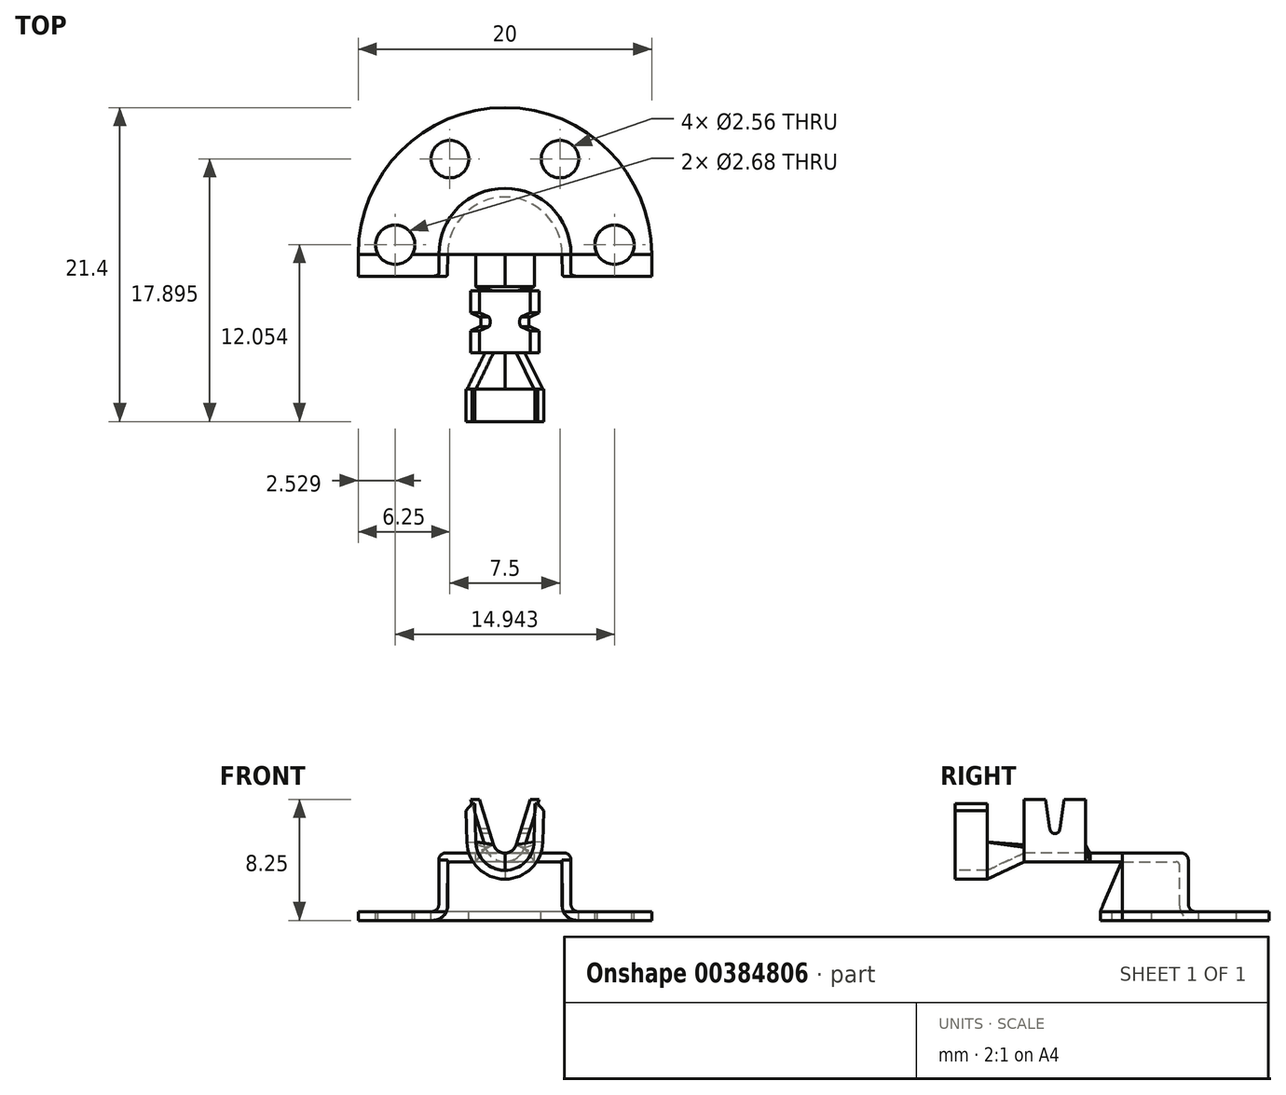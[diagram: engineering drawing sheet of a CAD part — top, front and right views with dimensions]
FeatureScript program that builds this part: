
annotation { "Feature Type Name" : "Feature", "Feature Type Description" : "" }
export const myFeature = defineFeature(function(context is Context, id is Id, definition is map)
    precondition{}
    {
        {
            var Q0;
            Q0=qCreatedBy(makeId("Front.planeOp"),FACE);
            var sketch = newSketch(context, id + "F0", { "sketchPlane" : qUnion([Q0])});
            skArc(sketch, "E0", {"start": v(-1.98, -0.05) * mm, "mid": v(0, -1.98) * mm, "end": v(1.98, -0.05) * mm});
            skArc(sketch, "E1", {"start": v(-2.58, -0.06) * mm, "mid": v(0, -2.58) * mm, "end": v(2.58, -0.06) * mm});
            skLineSegment(sketch, "E2", {"start": v(2.58, -0.06) * mm, "end": v(2.64, 2.08) * mm});
            skLineSegment(sketch, "E3", {"start": v(1.98, -0.05) * mm, "end": v(2.05, 2.57) * mm});
            skLineSegment(sketch, "E4", {"start": v(2.05, 2.57) * mm, "end": v(2.25, 2.56) * mm});
            skLineSegment(sketch, "E5.MirrorCS", {"start": v(-1.98, -0.05) * mm, "end": v(-2.05, 2.57) * mm});
            skLineSegment(sketch, "E6.MirrorCS", {"start": v(-2.58, -0.06) * mm, "end": v(-2.64, 2.08) * mm});
            skLineSegment(sketch, "E7.MirrorCS", {"start": v(-2.25, 2.56) * mm, "end": v(-2.64, 2.08) * mm});
            skLineSegment(sketch, "E8.MirrorCS", {"start": v(-2.05, 2.57) * mm, "end": v(-2.25, 2.56) * mm});
            skPoint(sketch, "E9", {"position": v(0, -2.58) * mm});
            skLineSegment(sketch, "E10", {"start": v(2.25, 2.56) * mm, "end": v(2.64, 2.08) * mm});
            skSolve(sketch);
        }
        {
            var Q0;
            Q0=makeQuery(id+"F0.imprint","IMPRINT",FACE,{"disambiguationData":[TD([[makeQuery(id+"F0.imprint","IMPRINT",EDGE,{"derivedFrom":sQuery(id+"F0.wireOp",EDGE,"E0")}),-1.0]])]});
            extrude(context, id + "F1", {"entities" : qUnion([Q0]), "oppositeDirection" : true, "depth" : 2.2 * mm});
        }
        {
            var Q0;
            Q0=makeQuery(id+"F1.opExtrude","CAP_FACE",FACE,{"disambiguationData":[OSD([sQuery(id+"F0.wireOp",EDGE,"E0"),sQuery(id+"F0.wireOp",EDGE,"E1"),sQuery(id+"F0.wireOp",EDGE,"E2"),sQuery(id+"F0.wireOp",EDGE,"E3"),sQuery(id+"F0.wireOp",EDGE,"E4"),sQuery(id+"F0.wireOp",EDGE,"E5.MirrorCS"),sQuery(id+"F0.wireOp",EDGE,"E6.MirrorCS"),sQuery(id+"F0.wireOp",EDGE,"E7.MirrorCS"),sQuery(id+"F0.wireOp",EDGE,"E8.MirrorCS"),sQuery(id+"F0.wireOp",EDGE,"E10")])],"isStart":false});
            cPlane(context, id + "F2", {"entities" : qUnion([Q0]), "cplaneType" : CPlaneType.OFFSET, "offset" : 2.5 * mm, "width" : 150 * mm, "height" : 150 * mm});
        }
        {
            var Q0;
            Q0=qCreatedBy(id+"F2.planeOp",FACE);
            var sketch = newSketch(context, id + "F3", { "sketchPlane" : qUnion([Q0])});
            skArc(sketch, "E11.converted", {"start": v(-0.77, -0.24) * mm, "mid": v(0, -0.8) * mm, "end": v(0.77, -0.24) * mm});
            skArc(sketch, "E12.converted", {"start": v(-1.34, -0.41) * mm, "mid": v(0, -1.4) * mm, "end": v(1.34, -0.41) * mm});
            skLineSegment(sketch, "E13", {"start": v(1.34, -0.41) * mm, "end": v(2.34, 2.85) * mm});
            skLineSegment(sketch, "E14", {"start": v(0.77, -0.24) * mm, "end": v(1.73, 2.85) * mm});
            skLineSegment(sketch, "E15", {"start": v(1.72, 2.85) * mm, "end": v(2.34, 2.85) * mm});
            skLineSegment(sketch, "E16", {"start": v(-2.74, -1.4) * mm, "end": v(2.74, -1.4) * mm, "construction": true});
            skLineSegment(sketch, "E17.MirrorCS", {"start": v(-0.77, -0.24) * mm, "end": v(-1.73, 2.85) * mm});
            skLineSegment(sketch, "E18.MirrorCS", {"start": v(-1.34, -0.41) * mm, "end": v(-2.34, 2.85) * mm});
            skLineSegment(sketch, "E19.MirrorCS", {"start": v(-1.72, 2.85) * mm, "end": v(-2.34, 2.85) * mm});
            skPoint(sketch, "E20.orphan", {"position": v(2.1, 2.04) * mm});
            skPoint(sketch, "E21.orphan", {"position": v(-2.1, 2.04) * mm});
            skSolve(sketch);
        }
        {
            var Q0;
            Q0=qSketchRegion(id+"F3",true);
            extrude(context, id + "F4", {"entities" : qUnion([Q0]), "depth" : 4.2 * mm});
        }
        {
            var Q0;
            Q0=makeQuery(id+"F4.opExtrude","CAP_FACE",FACE,{"disambiguationData":[OSD([sQuery(id+"F3.wireOp",EDGE,"E11.converted"),sQuery(id+"F3.wireOp",EDGE,"E12.converted"),sQuery(id+"F3.wireOp",EDGE,"E13"),sQuery(id+"F3.wireOp",EDGE,"E14"),sQuery(id+"F3.wireOp",EDGE,"E15"),sQuery(id+"F3.wireOp",EDGE,"JUiI4d2J-rTaX-Cvjk-MSou-KpunC5FrSqzR"),sQuery(id+"F3.wireOp",EDGE,"E17.MirrorCS"),sQuery(id+"F3.wireOp",EDGE,"E18.MirrorCS"),sQuery(id+"F3.wireOp",EDGE,"aa090b4b-4b93-4f69-ac82-eb0763e6126e0.MirrorCS"),sQuery(id+"F3.wireOp",EDGE,"E19.MirrorCS")])],"isStart":true});
            var sketch = newSketch(context, id + "F5", { "sketchPlane" : qUnion([Q0])});
            skArc(sketch, "E22", {"start": v(0, -0.81) * mm, "mid": v(0.48, -0.65) * mm, "end": v(0.77, -0.24) * mm});
            skArc(sketch, "E23", {"start": v(0, -1.41) * mm, "mid": v(0.84, -1.13) * mm, "end": v(1.35, -0.41) * mm});
            skLineSegment(sketch, "E24", {"start": v(0.77, -0.24) * mm, "end": v(1.35, -0.41) * mm});
            skLineSegment(sketch, "E25", {"start": v(0, 0) * mm, "end": v(0, -1.92) * mm, "construction": true});
            skLineSegment(sketch, "E26", {"start": v(0, -0.81) * mm, "end": v(0, -1.41) * mm});
            skSolve(sketch);
        }
        {
            var Q0;
            Q0=makeQuery(id+"F1.opExtrude","CAP_FACE",FACE,{"disambiguationData":[OSD([sQuery(id+"F0.wireOp",EDGE,"E0"),sQuery(id+"F0.wireOp",EDGE,"E1"),sQuery(id+"F0.wireOp",EDGE,"E2"),sQuery(id+"F0.wireOp",EDGE,"E3"),sQuery(id+"F0.wireOp",EDGE,"E4"),sQuery(id+"F0.wireOp",EDGE,"E5.MirrorCS"),sQuery(id+"F0.wireOp",EDGE,"E6.MirrorCS"),sQuery(id+"F0.wireOp",EDGE,"E7.MirrorCS"),sQuery(id+"F0.wireOp",EDGE,"E8.MirrorCS"),sQuery(id+"F0.wireOp",EDGE,"E10")])],"isStart":false});
            var sketch = newSketch(context, id + "F6", { "sketchPlane" : qUnion([Q0])});
            skArc(sketch, "E27", {"start": v(-1.98, -0.05) * mm, "mid": v(-1.39, -1.42) * mm, "end": v(0, -1.98) * mm});
            skArc(sketch, "E28", {"start": v(-2.58, -0.06) * mm, "mid": v(-1.8, -1.85) * mm, "end": v(0, -2.58) * mm});
            skLineSegment(sketch, "E29", {"start": v(-2.58, -0.06) * mm, "end": v(-1.98, -0.05) * mm});
            skLineSegment(sketch, "E30", {"start": v(0, 0) * mm, "end": v(0, -2.84) * mm, "construction": true});
            skPoint(sketch, "E30.endSnap0", {"position": v(0, -1.98) * mm});
            skLineSegment(sketch, "E31", {"start": v(0, -1.99) * mm, "end": v(0, -2.58) * mm});
            skSolve(sketch);
        }
        {
            var Q0;
            Q0=qSketchRegion(id+"F5",true);
            var Q1;
            Q1=qSketchRegion(id+"F6",true);
            loft(context, id + "F7", {"sheetProfilesArray" : [{ "sheetProfileEntities" : qUnion([Q0]) }, { "sheetProfileEntities" : qUnion([Q1]) }]});
        }
        {
            var Q0;
            {var subQ0=sQuery(id+"F5.wireOp",EDGE,"E23");Q0=makeQuery(id+"F7.opLoft","SWEPT_BODY",BODY,{"disambiguationData":[OSD([makeQuery(id+"F5.imprint","IMPRINT",FACE,{"disambiguationData":[TD([[makeQuery(id+"F5.imprint","IMPRINT",EDGE,{"derivedFrom":subQ0}),1.0]])]}),makeQuery(id+"F6.imprint","IMPRINT",FACE,{"disambiguationData":[TD([[makeQuery(id+"F6.imprint","IMPRINT",EDGE,{"derivedFrom":sQuery(id+"F6.wireOp",EDGE,"E27")}),1.0]])]})])]});}
            var Q1;
            Q1=qCreatedBy(makeId("Right.planeOp"),FACE);
            mirror(context, id + "F8", {"entities" : qUnion([Q0]), "mirrorPlane" : qUnion([Q1])});
        }
        {
            var Q0;
            Q0=makeQuery(id+"F4.opExtrude","CAP_FACE",FACE,{"disambiguationData":[OSD([sQuery(id+"F3.wireOp",EDGE,"E11.converted"),sQuery(id+"F3.wireOp",EDGE,"E12.converted"),sQuery(id+"F3.wireOp",EDGE,"E13"),sQuery(id+"F3.wireOp",EDGE,"E14"),sQuery(id+"F3.wireOp",EDGE,"E15"),sQuery(id+"F3.wireOp",EDGE,"JUiI4d2J-rTaX-Cvjk-MSou-KpunC5FrSqzR"),sQuery(id+"F3.wireOp",EDGE,"E17.MirrorCS"),sQuery(id+"F3.wireOp",EDGE,"E18.MirrorCS"),sQuery(id+"F3.wireOp",EDGE,"aa090b4b-4b93-4f69-ac82-eb0763e6126e0.MirrorCS"),sQuery(id+"F3.wireOp",EDGE,"E19.MirrorCS")])],"isStart":false});
            cPlane(context, id + "F9", {"entities" : qUnion([Q0]), "cplaneType" : CPlaneType.OFFSET, "offset" : .3 * mm, "width" : 150 * mm, "height" : 150 * mm});
        }
        {
            var Q0;
            Q0=qCreatedBy(id+"F9.planeOp",FACE);
            var sketch = newSketch(context, id + "F10", { "sketchPlane" : qUnion([Q0])});
            skLineSegment(sketch, "E32", {"start": v(0, -0.8) * mm, "end": v(0, -1.4) * mm, "construction": true});
            skLineSegment(sketch, "E33", {"start": v(0, -0.8) * mm, "end": v(0, -1.4) * mm});
            skLineSegment(sketch, "E34.MirrorCS", {"start": v(0, -1.4) * mm, "end": v(2, -1.4) * mm});
            skLineSegment(sketch, "E35.MirrorCS", {"start": v(2, -1.4) * mm, "end": v(2, -0.8) * mm});
            skLineSegment(sketch, "E36.MirrorCS", {"start": v(0, -0.8) * mm, "end": v(2, -0.8) * mm});
            skSolve(sketch);
        }
        {
            var Q0;
            Q0=makeQuery(id+"F4.opExtrude","CAP_FACE",FACE,{"disambiguationData":[OSD([sQuery(id+"F3.wireOp",EDGE,"E11.converted"),sQuery(id+"F3.wireOp",EDGE,"E12.converted"),sQuery(id+"F3.wireOp",EDGE,"E13"),sQuery(id+"F3.wireOp",EDGE,"E14"),sQuery(id+"F3.wireOp",EDGE,"E15"),sQuery(id+"F3.wireOp",EDGE,"JUiI4d2J-rTaX-Cvjk-MSou-KpunC5FrSqzR"),sQuery(id+"F3.wireOp",EDGE,"E17.MirrorCS"),sQuery(id+"F3.wireOp",EDGE,"E18.MirrorCS"),sQuery(id+"F3.wireOp",EDGE,"aa090b4b-4b93-4f69-ac82-eb0763e6126e0.MirrorCS"),sQuery(id+"F3.wireOp",EDGE,"E19.MirrorCS")])],"isStart":false});
            var sketch = newSketch(context, id + "F11", { "sketchPlane" : qUnion([Q0])});
            skLineSegment(sketch, "E37", {"start": v(0, 0) * mm, "end": v(0, -1.83) * mm, "construction": true});
            skPoint(sketch, "E37.endSnap0", {"position": v(0, -0.8) * mm});
            skLineSegment(sketch, "E38", {"start": v(0, -0.81) * mm, "end": v(0, -1.41) * mm});
            skLineSegment(sketch, "E39.MirrorCS", {"start": v(0.77, -0.25) * mm, "end": v(1.35, -0.41) * mm});
            skArc(sketch, "E40", {"start": v(0, -0.81) * mm, "mid": v(0.48, -0.66) * mm, "end": v(0.77, -0.25) * mm});
            skArc(sketch, "E41", {"start": v(0, -1.41) * mm, "mid": v(0.84, -1.13) * mm, "end": v(1.35, -0.41) * mm});
            skSolve(sketch);
        }
        {
            var Q0;
            Q0=qSketchRegion(id+"F11",true);
            var Q1;
            Q1=qSketchRegion(id+"F10",true);
            loft(context, id + "F12", {"sheetProfilesArray" : [{ "sheetProfileEntities" : qUnion([Q0]) }, { "sheetProfileEntities" : qUnion([Q1]) }]});
        }
        {
            var Q0;
            {var subQ0=sQuery(id+"F11.wireOp",EDGE,"E41");Q0=makeQuery(id+"F12.opLoft","SWEPT_BODY",BODY,{"disambiguationData":[OSD([makeQuery(id+"F10.imprint","IMPRINT",FACE,{"disambiguationData":[TD([[makeQuery(id+"F10.imprint","IMPRINT",EDGE,{"derivedFrom":sQuery(id+"F10.wireOp",EDGE,"E33")}),1.0]])]}),makeQuery(id+"F11.imprint","IMPRINT",FACE,{"disambiguationData":[TD([[makeQuery(id+"F11.imprint","IMPRINT",EDGE,{"derivedFrom":subQ0}),1.0]])]})])]});}
            var Q1;
            Q1=qCreatedBy(makeId("Right.planeOp"),FACE);
            mirror(context, id + "F13", {"entities" : qUnion([Q0]), "mirrorPlane" : qUnion([Q1])});
        }
        {
            var Q0;
            Q0=makeQuery(id+"F10.imprint","IMPRINT",FACE,{"disambiguationData":[TD([[makeQuery(id+"F10.imprint","IMPRINT",EDGE,{"derivedFrom":sQuery(id+"F10.wireOp",EDGE,"E33")}),1.0]])]});
            cPlane(context, id + "F14", {"entities" : qUnion([Q0]), "cplaneType" : CPlaneType.OFFSET, "offset" : 2.2 * mm, "width" : 150 * mm, "height" : 150 * mm});
        }
        {
            var Q0;
            Q0=qCreatedBy(id+"F14.planeOp",FACE);
            var sketch = newSketch(context, id + "F15", { "sketchPlane" : qUnion([Q0])});
            skLineSegment(sketch, "E42", {"start": v(0, 0) * mm, "end": v(0, -2.78) * mm, "construction": true});
            skLineSegment(sketch, "E43", {"start": v(0, -0.8) * mm, "end": v(2, -0.8) * mm});
            skLineSegment(sketch, "E44", {"start": v(0, -1.4) * mm, "end": v(2, -1.4) * mm});
            skLineSegment(sketch, "E45", {"start": v(2, -1.4) * mm, "end": v(2, -0.8) * mm});
            skLineSegment(sketch, "E46", {"start": v(0, -0.8) * mm, "end": v(0, -1.4) * mm});
            skSolve(sketch);
        }
        {
            var Q1;
            Q1=qSketchRegion(id+"F10",true);
            var Q2;
            Q2=qSketchRegion(id+"F15",true);
            loft(context, id + "F16", {"operationType" : NewBodyOperationType.ADD, "sheetProfilesArray" : [{ "sheetProfileEntities" : qUnion([Q1]) }, { "sheetProfileEntities" : qUnion([Q2]) }]});
        }
        {
            var Q0;
            {var subQ0=sQuery(id+"F11.wireOp",EDGE,"E41");Q0=makeQuery(id+"F12.opLoft","SWEPT_BODY",BODY,{"disambiguationData":[OSD([makeQuery(id+"F10.imprint","IMPRINT",FACE,{"disambiguationData":[TD([[makeQuery(id+"F10.imprint","IMPRINT",EDGE,{"derivedFrom":sQuery(id+"F10.wireOp",EDGE,"E33")}),1.0]])]}),makeQuery(id+"F11.imprint","IMPRINT",FACE,{"disambiguationData":[TD([[makeQuery(id+"F11.imprint","IMPRINT",EDGE,{"derivedFrom":subQ0}),1.0]])]})])]});}
            var Q1;
            Q1=qCreatedBy(makeId("Right.planeOp"),FACE);
            mirror(context, id + "F17", {"entities" : qUnion([Q0]), "mirrorPlane" : qUnion([Q1])});
        }
        {
            var Q0;
            Q0=makeQuery(id+"F16.opLoft","CAP_FACE",FACE,{"disambiguationData":[OSD([makeQuery(id+"F15.imprint","IMPRINT",FACE,{"disambiguationData":[TD([[makeQuery(id+"F15.imprint","IMPRINT",EDGE,{"derivedFrom":sQuery(id+"F15.wireOp",EDGE,"E43")}),-1.0]])]})])],"isStart":true});
            var sketch = newSketch(context, id + "F18", { "sketchPlane" : qUnion([Q0])});
            skLineSegment(sketch, "E47.bottom", {"start": v(2, -1.4) * mm, "end": v(0, -1.4) * mm});
            skLineSegment(sketch, "E47.top", {"start": v(2.5, -0.8) * mm, "end": v(0, -0.8) * mm});
            skLineSegment(sketch, "E48", {"start": v(0, 0) * mm, "end": v(0, -3.86) * mm, "construction": true});
            skLineSegment(sketch, "E49", {"start": v(2.5, -0.8) * mm, "end": v(2, -1.4) * mm});
            skLineSegment(sketch, "E50", {"start": v(2.5, -0.8) * mm, "end": v(4, -0.8) * mm});
            skLineSegment(sketch, "E51", {"start": v(4.5, -1.3) * mm, "end": v(4.5, -4.3) * mm});
            skLineSegment(sketch, "E52", {"start": v(5, -4.8) * mm, "end": v(10, -4.8) * mm});
            skPoint(sketch, "E53.visualSharp", {"position": v(4.5, -0.8) * mm});
            skArc(sketch, "E53.filletArc", {"start": v(4.5, -1.3) * mm, "mid": v(4.35, -0.95) * mm, "end": v(4, -0.8) * mm});
            skPoint(sketch, "E54.visualSharp", {"position": v(4.5, -4.8) * mm});
            skArc(sketch, "E54.filletArc", {"start": v(4.5, -4.3) * mm, "mid": v(4.65, -4.65) * mm, "end": v(5, -4.8) * mm});
            skLineSegment(sketch, "E55.0", {"start": v(2, -1.4) * mm, "end": v(3.65, -1.4) * mm});
            skLineSegment(sketch, "E56.0", {"start": v(3.9, -1.65) * mm, "end": v(3.9, -4.4) * mm});
            skArc(sketch, "E57.filletArc", {"start": v(3.9, -1.65) * mm, "mid": v(3.83, -1.47) * mm, "end": v(3.65, -1.4) * mm});
            skLineSegment(sketch, "E58.0", {"start": v(4.9, -5.4) * mm, "end": v(10, -5.4) * mm});
            skArc(sketch, "E59.filletArc", {"start": v(3.9, -4.4) * mm, "mid": v(4.2, -5.1) * mm, "end": v(4.9, -5.4) * mm});
            skLineSegment(sketch, "E60", {"start": v(10, -4.8) * mm, "end": v(10, -5.4) * mm});
            skLineSegment(sketch, "E61", {"start": v(0, -0.8) * mm, "end": v(0, -1.4) * mm});
            skSolve(sketch);
        }
        {
            var Q0;
            Q0=makeQuery(id+"F18.imprint","IMPRINT",FACE,{"disambiguationData":[TD([[makeQuery(id+"F18.imprint","IMPRINT",EDGE,{"derivedFrom":sQuery(id+"F18.wireOp",EDGE,"E47.bottom")}),1.0]])]});
            var sketch = newSketch(context, id + "F19", { "sketchPlane" : qUnion([Q0])});
            skLineSegment(sketch, "E62", {"start": v(0, 0) * mm, "end": v(0, -4.76) * mm});
            skSolve(sketch);
        }
        {
            var Q0;
            Q0=qSketchRegion(id+"F18",true);
            var Q1;
            Q1=sQuery(id+"F19.wireOp",EDGE,"E62");
            revolve(context, id + "F20", {"entities" : qUnion([Q0]), "axis" : qUnion([Q1]), "revolveType" : RevolveType.ONE_DIRECTION, "angle" : 180 * degree});
        }
        {
            var Q0;
            Q0=makeQuery(id+"F20.opRevolve","CAP_FACE",FACE,{"disambiguationData":[OSD([sQuery(id+"F18.wireOp",EDGE,"E47.bottom"),sQuery(id+"F18.wireOp",EDGE,"E47.top"),sQuery(id+"F18.wireOp",EDGE,"E50"),sQuery(id+"F18.wireOp",EDGE,"E51"),sQuery(id+"F18.wireOp",EDGE,"E52"),sQuery(id+"F18.wireOp",EDGE,"E53.filletArc"),sQuery(id+"F18.wireOp",EDGE,"E54.filletArc"),sQuery(id+"F18.wireOp",EDGE,"E55.0"),sQuery(id+"F18.wireOp",EDGE,"E56.0"),sQuery(id+"F18.wireOp",EDGE,"E57.filletArc"),sQuery(id+"F18.wireOp",EDGE,"E58.0"),sQuery(id+"F18.wireOp",EDGE,"E59.filletArc"),sQuery(id+"F18.wireOp",EDGE,"E60"),sQuery(id+"F18.wireOp",EDGE,"E61")])],"isStart":false});
            var sketch = newSketch(context, id + "F21", { "sketchPlane" : qUnion([Q0])});
            skLineSegment(sketch, "E63.bottom", {"start": v(-10, -4.8) * mm, "end": v(-5, -4.8) * mm});
            skLineSegment(sketch, "E63.top", {"start": v(-10, -5.4) * mm, "end": v(-4.9, -5.4) * mm});
            skLineSegment(sketch, "E63.left", {"start": v(-10, -4.8) * mm, "end": v(-10, -5.4) * mm});
            skLineSegment(sketch, "E64", {"start": v(-4.5, -1.3) * mm, "end": v(-4.5, -4.3) * mm});
            skLineSegment(sketch, "E65", {"start": v(-3.9, -4.4) * mm, "end": v(-3.9, -1.3) * mm});
            skLineSegment(sketch, "E66", {"start": v(-4.5, -1.3) * mm, "end": v(-3.9, -1.3) * mm});
            skPoint(sketch, "E67.orphan", {"position": v(-3.9, -1.15) * mm});
            skPoint(sketch, "E68.visualSharp", {"position": v(-4.5, -4.8) * mm});
            skArc(sketch, "E68.filletArc", {"start": v(-5, -4.8) * mm, "mid": v(-4.65, -4.65) * mm, "end": v(-4.5, -4.3) * mm});
            skPoint(sketch, "E69.visualSharp", {"position": v(-3.91, -5.4) * mm});
            skArc(sketch, "E69.filletArc", {"start": v(-4.9, -5.4) * mm, "mid": v(-4.2, -5.1) * mm, "end": v(-3.9, -4.4) * mm});
            skSolve(sketch);
        }
        {
            var Q0;
            Q0=qSketchRegion(id+"F21",true);
            extrude(context, id + "F22", {"entities" : qUnion([Q0]), "operationType" : NewBodyOperationType.ADD, "depth" : 1.5 * mm});
        }
        {
            var Q0;
            Q0=makeQuery(id+"F22.opExtrude","SWEPT_FACE",FACE,{"disambiguationData":[OSD([sQuery(id+"F21.wireOp",EDGE,"E64")])]});
            var sketch = newSketch(context, id + "F23", { "sketchPlane" : qUnion([Q0])});
            skLineSegment(sketch, "E70", {"start": v(-11.4, -1.3) * mm, "end": v(-9.9, -4.8) * mm});
            skLineSegment(sketch, "E71", {"start": v(-11.4, -1.3) * mm, "end": v(-9.9, -1.3) * mm});
            skLineSegment(sketch, "E72", {"start": v(-9.9, -1.3) * mm, "end": v(-9.9, -4.8) * mm});
            skSolve(sketch);
        }
        {
            var Q0;
            Q0=qSketchRegion(id+"F23",true);
            extrude(context, id + "F24", {"entities" : qUnion([Q0]), "operationType" : NewBodyOperationType.REMOVE, "depth" : 1 * mm, "hasSecondDirection" : true, "secondDirectionOppositeDirection" : true, "secondDirectionDepth" : 0.9 * mm});
        }
        {
            var Q0;
            Q0=makeQuery(id+"F20.opRevolve","SWEPT_BODY",BODY,{"disambiguationData":[OSD([sQuery(id+"F18.wireOp",EDGE,"E47.bottom"),sQuery(id+"F18.wireOp",EDGE,"E47.top"),sQuery(id+"F18.wireOp",EDGE,"E50"),sQuery(id+"F18.wireOp",EDGE,"E51"),sQuery(id+"F18.wireOp",EDGE,"E52"),sQuery(id+"F18.wireOp",EDGE,"E53.filletArc"),sQuery(id+"F18.wireOp",EDGE,"E54.filletArc"),sQuery(id+"F18.wireOp",EDGE,"E55.0"),sQuery(id+"F18.wireOp",EDGE,"E56.0"),sQuery(id+"F18.wireOp",EDGE,"E57.filletArc"),sQuery(id+"F18.wireOp",EDGE,"E58.0"),sQuery(id+"F18.wireOp",EDGE,"E59.filletArc"),sQuery(id+"F18.wireOp",EDGE,"E60"),sQuery(id+"F18.wireOp",EDGE,"E61")])]});
            var Q1;
            Q1=qCreatedBy(makeId("Right.planeOp"),FACE);
            mirror(context, id + "F25", {"entities" : qUnion([Q0]), "mirrorPlane" : qUnion([Q1])});
        }
        {
            var Q0;
            Q0=makeQuery(id+"F22.boolean.opBoolean","MERGE",FACE,{"derivedFrom":[makeQuery(id+"F20.opRevolve","SWEPT_FACE",FACE,{"disambiguationData":[OSD([sQuery(id+"F18.wireOp",EDGE,"E52")])]}),makeQuery(id+"F22.opExtrude","SWEPT_FACE",FACE,{"disambiguationData":[OSD([sQuery(id+"F21.wireOp",EDGE,"E63.bottom")])]})]});
            var sketch = newSketch(context, id + "F26", { "sketchPlane" : qUnion([Q0])});
            skArc(sketch, "E73", {"start": v(7.5, 11.4) * mm, "mid": v(0, 18.9) * mm, "end": v(-7.5, 11.4) * mm, "construction": true});
            skLineSegment(sketch, "E74", {"start": v(0, 11.4) * mm, "end": v(-9.29, 12.21) * mm, "construction": true});
            skCircle(sketch, "E75", {"center": v(-7.47, 12.05) * mm, "radius": 1.34 * mm});
            skLineSegment(sketch, "E76", {"start": v(0, 11.4) * mm, "end": v(-4.6, 19.38) * mm, "construction": true});
            skCircle(sketch, "E77", {"center": v(-3.75, 17.9) * mm, "radius": 1.28 * mm});
            skLineSegment(sketch, "E78", {"start": v(0, 6.42) * mm, "end": v(0, 21.4) * mm, "construction": true});
            skCircle(sketch, "E79.MirrorC", {"center": v(3.75, 17.9) * mm, "radius": 1.28 * mm});
            skCircle(sketch, "E80.MirrorC", {"center": v(7.47, 12.05) * mm, "radius": 1.34 * mm});
            skSolve(sketch);
        }
        {
            var Q0;
            Q0=qSketchRegion(id+"F26",true);
            extrude(context, id + "F27", {"entities" : qUnion([Q0]), "operationType" : NewBodyOperationType.REMOVE, "endBound" : BoundingType.THROUGH_ALL, "oppositeDirection" : true, "depth" : 1 * mm});
        }
        {
            var Q0;
            Q0=makeQuery(id+"F16.opLoft","SWEPT_FACE",FACE,{"disambiguationData":[OSD([sQuery(id+"F10.wireOp",EDGE,"E34.MirrorCS"),sQuery(id+"F10.wireOp",EDGE,"E35.MirrorCS"),sQuery(id+"F10.wireOp",EDGE,"E36.MirrorCS"),sQuery(id+"F15.wireOp",EDGE,"E43"),sQuery(id+"F15.wireOp",EDGE,"E44"),sQuery(id+"F15.wireOp",EDGE,"E45")])]});
            var sketch = newSketch(context, id + "F28", { "sketchPlane" : qUnion([Q0])});
            skLineSegment(sketch, "E81", {"start": v(-8.9, 2.85) * mm, "end": v(-4.7, 2.85) * mm});
            skLineSegment(sketch, "E82", {"start": v(-8.9, 2.85) * mm, "end": v(-8.9, 0) * mm});
            skLineSegment(sketch, "E83", {"start": v(-4.7, 2.85) * mm, "end": v(-4.7, 0) * mm});
            skLineSegment(sketch, "E84", {"start": v(-6.8, 2.85) * mm, "end": v(-6.8, 0.25) * mm, "construction": true});
            skLineSegment(sketch, "E85", {"start": v(-7.42, 2.85) * mm, "end": v(-7.13, 0.77) * mm});
            skLineSegment(sketch, "E86", {"start": v(-6.18, 2.85) * mm, "end": v(-6.47, 0.76) * mm});
            skArc(sketch, "E87", {"start": v(-7.14, 0.84) * mm, "mid": v(-6.8, 0.51) * mm, "end": v(-6.46, 0.85) * mm});
            skSolve(sketch);
        }
        {
            var Q0;
            Q0=qSketchRegion(id+"F28",true);
            extrude(context, id + "F29", {"entities" : qUnion([Q0]), "operationType" : NewBodyOperationType.REMOVE, "oppositeDirection" : true, "depth" : 25 * mm, "hasSecondDirection" : true, "secondDirectionOppositeDirection" : false, "secondDirectionDepth" : 25 * mm});
        }
    });
